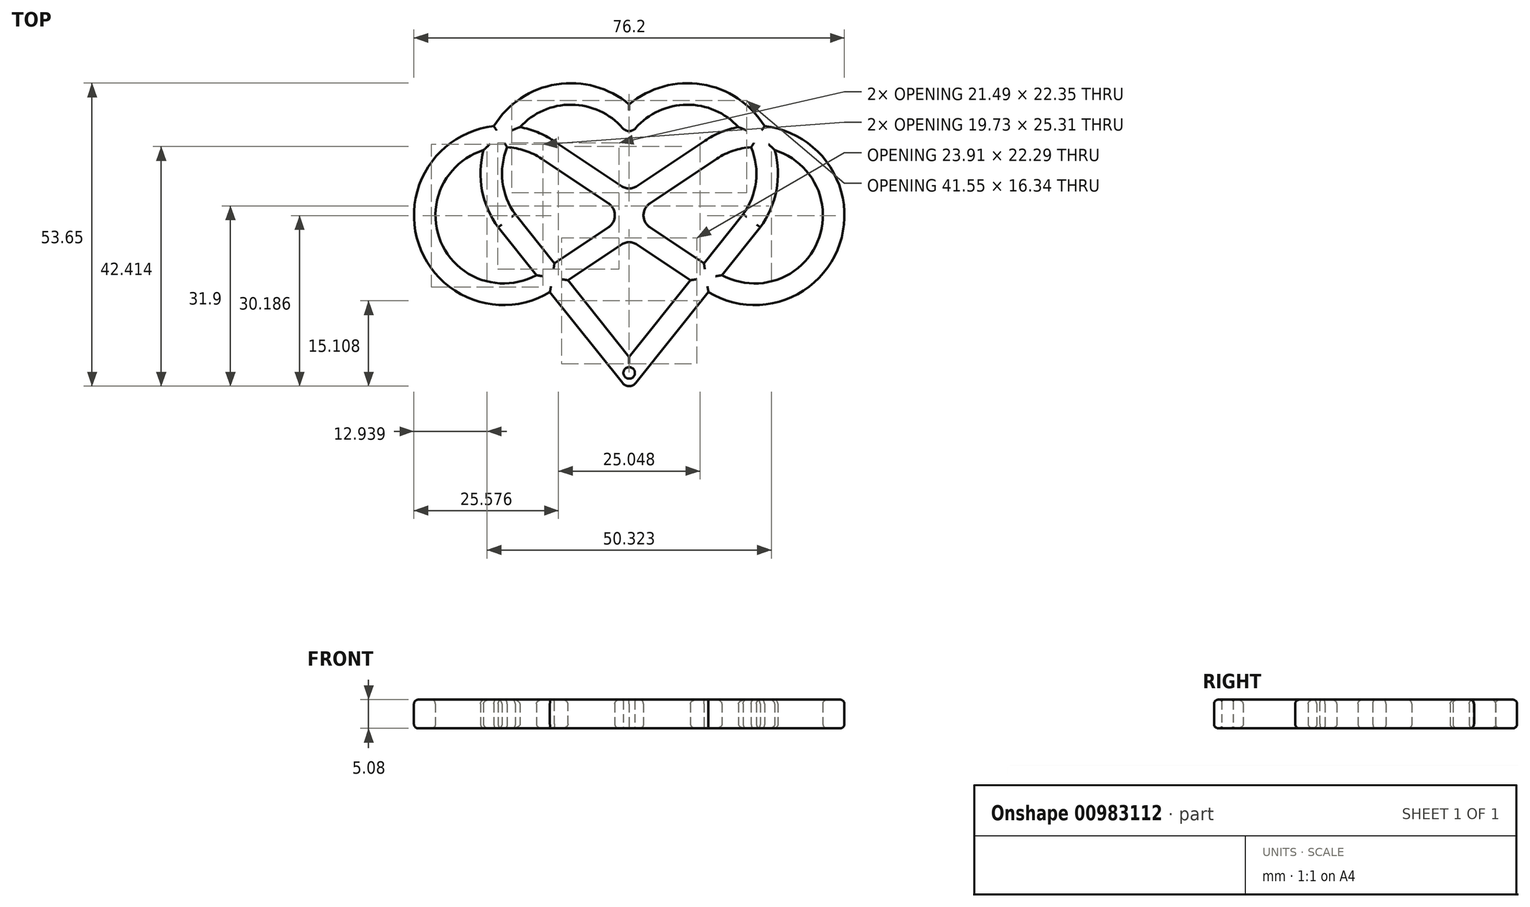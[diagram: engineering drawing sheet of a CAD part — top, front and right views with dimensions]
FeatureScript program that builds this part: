
annotation { "Feature Type Name" : "Feature", "Feature Type Description" : "" }
export const myFeature = defineFeature(function(context is Context, id is Id, definition is map)
    precondition{}
    {
        {
            var Q0;
            Q0=qCreatedBy(makeId("Top.planeOp"),FACE);
            var sketch = newSketch(context, id + "F0", { "sketchPlane" : qUnion([Q0])});
            skLineSegment(sketch, "E0", {"start": v(-12.42, -31.73) * mm, "end": v(-12.42, 29.15) * mm, "construction": true});
            skArc(sketch, "E1.0", {"start": v(-12.42, 24.7) * mm, "mid": v(-33.69, 24.13) * mm, "end": v(-35.61, 2.94) * mm});
            skArc(sketch, "E1.1", {"start": v(-12.42, 24.7) * mm, "mid": v(8.85, 24.13) * mm, "end": v(10.77, 2.94) * mm});
            skLineSegment(sketch, "E1.2", {"start": v(10.77, 2.94) * mm, "end": v(-12.42, -26.1) * mm});
            skLineSegment(sketch, "E1.3", {"start": v(-35.61, 2.94) * mm, "end": v(-12.42, -26.1) * mm});
            skArc(sketch, "E2.0", {"start": v(-12.42, 18.97) * mm, "mid": v(-29.6, 22.55) * mm, "end": v(-32.59, 5.26) * mm});
            skArc(sketch, "E2.1", {"start": v(-12.42, 18.97) * mm, "mid": v(4.75, 22.55) * mm, "end": v(7.75, 5.26) * mm});
            skLineSegment(sketch, "E2.2", {"start": v(7.75, 5.26) * mm, "end": v(-12.42, -20) * mm});
            skLineSegment(sketch, "E2.3", {"start": v(-32.59, 5.26) * mm, "end": v(-12.42, -20) * mm});
            skSolve(sketch);
        }
        {
            var Q0;
            Q0 = qSketchRegion(id + "F0", true);
            extrude(context, id + "F1", {"entities" : qUnion([Q0]), "depth" : 5.08 * mm, "offsetDistance" : 25.4 * mm});
        }
        {
            var Q0;
            Q0=qCreatedBy(makeId("Top.planeOp"),FACE);
            var sketch = newSketch(context, id + "F2", { "sketchPlane" : qUnion([Q0])});
            skArc(sketch, "E3", {"start": v(0.99, -8.13) * mm, "mid": v(25.68, 5.07) * mm, "end": v(0.99, 18.27) * mm});
            skLineSegment(sketch, "E4", {"start": v(-12.42, 45.5) * mm, "end": v(-12.42, -37.96) * mm, "construction": true});
            skArc(sketch, "E5.MirrorC", {"start": v(-25.83, -8.13) * mm, "mid": v(-50.52, 5.07) * mm, "end": v(-25.83, 18.27) * mm});
            skLineSegment(sketch, "E6", {"start": v(-25.83, 18.27) * mm, "end": v(-34.64, 5.07) * mm, "construction": true});
            skLineSegment(sketch, "E7", {"start": v(-34.64, 5.07) * mm, "end": v(9.8, 5.07) * mm, "construction": true});
            skLineSegment(sketch, "E8", {"start": v(-25.83, 18.27) * mm, "end": v(-12.42, 9.31) * mm});
            skLineSegment(sketch, "E9.MirrorCS", {"start": v(-25.83, -8.13) * mm, "end": v(-12.42, 0.82) * mm});
            skLineSegment(sketch, "E10.MirrorCS", {"start": v(0.99, 18.27) * mm, "end": v(-12.42, 9.31) * mm});
            skLineSegment(sketch, "E11.MirrorCS", {"start": v(0.99, -8.13) * mm, "end": v(-12.42, 0.82) * mm});
            skPoint(sketch, "E12.orphan", {"position": v(-18.77, 5.07) * mm});
            skPoint(sketch, "E13.orphan", {"position": v(-6.07, 5.07) * mm});
            skLineSegment(sketch, "E14.0", {"start": v(-27.94, -4.96) * mm, "end": v(-12.93, 5.07) * mm});
            skLineSegment(sketch, "E14.1", {"start": v(-27.94, 15.1) * mm, "end": v(-12.93, 5.07) * mm});
            skLineSegment(sketch, "E14.2", {"start": v(3.1, 15.1) * mm, "end": v(-11.91, 5.07) * mm});
            skArc(sketch, "E14.3", {"start": v(-27.94, -4.96) * mm, "mid": v(-46.7, 5.07) * mm, "end": v(-27.94, 15.1) * mm});
            skArc(sketch, "E14.4", {"start": v(3.1, -4.96) * mm, "mid": v(21.87, 5.07) * mm, "end": v(3.1, 15.1) * mm});
            skLineSegment(sketch, "E14.5", {"start": v(3.1, -4.96) * mm, "end": v(-11.91, 5.07) * mm});
            skSolve(sketch);
        }
        {
            var Q0;
            Q0 = qSketchRegion(id + "F2", true);
            extrude(context, id + "F3", {"entities" : qUnion([Q0]), "operationType" : NewBodyOperationType.ADD, "depth" : 5.08 * mm, "offsetDistance" : 25.4 * mm});
        }
        {
            var Q0;
            Q0=makeQuery(id+"F3.opExtrude","SWEPT_EDGE",EDGE,{"disambiguationData":[OSD([sQuery(id+"F2.wireOp",EDGE,"E14.2"),sQuery(id+"F2.wireOp",EDGE,"E14.5")])]});
            var Q1;
            Q1=makeQuery(id+"F3.opExtrude","SWEPT_EDGE",EDGE,{"disambiguationData":[OSD([sQuery(id+"F2.wireOp",EDGE,"E14.0"),sQuery(id+"F2.wireOp",EDGE,"E14.1")])]});
            var Q2;
            Q2=makeQuery(id+"F3.opExtrude","SWEPT_EDGE",EDGE,{"disambiguationData":[OSD([sQuery(id+"F2.wireOp",EDGE,"E8"),sQuery(id+"F2.wireOp",EDGE,"E10.MirrorCS")])]});
            var Q3;
            Q3=makeQuery(id+"F3.opExtrude","SWEPT_EDGE",EDGE,{"disambiguationData":[OSD([sQuery(id+"F2.wireOp",EDGE,"E9.MirrorCS"),sQuery(id+"F2.wireOp",EDGE,"E11.MirrorCS")])]});
            fillet(context, id + "F4", {"entities" : qUnion([Q0, Q1, Q2, Q3]), "radius" : 2.54 * mm, "tangentPropagation" : true, "allowEdgeOverflow" : false});
        }
        {
            var Q0;
            Q0=makeQuery(id+"F3.boolean.opBoolean","MERGE",FACE,{"derivedFrom":[makeQuery(id+"F1.opExtrude","CAP_FACE",FACE,{"disambiguationData":[OSD([sQuery(id+"F0.wireOp",EDGE,"E1.0"),sQuery(id+"F0.wireOp",EDGE,"E1.1"),sQuery(id+"F0.wireOp",EDGE,"E1.2"),sQuery(id+"F0.wireOp",EDGE,"E1.3"),sQuery(id+"F0.wireOp",EDGE,"E2.0"),sQuery(id+"F0.wireOp",EDGE,"E2.1"),sQuery(id+"F0.wireOp",EDGE,"E2.2"),sQuery(id+"F0.wireOp",EDGE,"E2.3")])],"isStart":false}),makeQuery(id+"F3.opExtrude","CAP_FACE",FACE,{"disambiguationData":[OSD([sQuery(id+"F2.wireOp",EDGE,"E3"),sQuery(id+"F2.wireOp",EDGE,"E5.MirrorC"),sQuery(id+"F2.wireOp",EDGE,"E8"),sQuery(id+"F2.wireOp",EDGE,"E9.MirrorCS"),sQuery(id+"F2.wireOp",EDGE,"E10.MirrorCS"),sQuery(id+"F2.wireOp",EDGE,"E11.MirrorCS"),sQuery(id+"F2.wireOp",EDGE,"E14.0"),sQuery(id+"F2.wireOp",EDGE,"E14.1"),sQuery(id+"F2.wireOp",EDGE,"E14.2"),sQuery(id+"F2.wireOp",EDGE,"E14.3"),sQuery(id+"F2.wireOp",EDGE,"E14.4"),sQuery(id+"F2.wireOp",EDGE,"E14.5")])],"isStart":false})]});
            var Q1;
            Q1=makeQuery(id+"F3.boolean.opBoolean","MERGE",FACE,{"derivedFrom":[makeQuery(id+"F1.opExtrude","CAP_FACE",FACE,{"disambiguationData":[OSD([sQuery(id+"F0.wireOp",EDGE,"E1.0"),sQuery(id+"F0.wireOp",EDGE,"E1.1"),sQuery(id+"F0.wireOp",EDGE,"E1.2"),sQuery(id+"F0.wireOp",EDGE,"E1.3"),sQuery(id+"F0.wireOp",EDGE,"E2.0"),sQuery(id+"F0.wireOp",EDGE,"E2.1"),sQuery(id+"F0.wireOp",EDGE,"E2.2"),sQuery(id+"F0.wireOp",EDGE,"E2.3")])],"isStart":true}),makeQuery(id+"F3.opExtrude","CAP_FACE",FACE,{"disambiguationData":[OSD([sQuery(id+"F2.wireOp",EDGE,"E3"),sQuery(id+"F2.wireOp",EDGE,"E5.MirrorC"),sQuery(id+"F2.wireOp",EDGE,"E8"),sQuery(id+"F2.wireOp",EDGE,"E9.MirrorCS"),sQuery(id+"F2.wireOp",EDGE,"E10.MirrorCS"),sQuery(id+"F2.wireOp",EDGE,"E11.MirrorCS"),sQuery(id+"F2.wireOp",EDGE,"E14.0"),sQuery(id+"F2.wireOp",EDGE,"E14.1"),sQuery(id+"F2.wireOp",EDGE,"E14.2"),sQuery(id+"F2.wireOp",EDGE,"E14.3"),sQuery(id+"F2.wireOp",EDGE,"E14.4"),sQuery(id+"F2.wireOp",EDGE,"E14.5")])],"isStart":true})]});
            fillet(context, id + "F5", {"entities" : qUnion([Q0, Q1]), "radius" : 0.76 * mm, "tangentPropagation" : true, "allowEdgeOverflow" : false});
        }
        {
            var Q0;
            Q0=qCreatedBy(makeId("Top.planeOp"),FACE);
            var sketch = newSketch(context, id + "F6", { "sketchPlane" : qUnion([Q0])});
            skCircle(sketch, "E15", {"center": v(-12.42, -22.83) * mm, "radius": 1.02 * mm});
            skSolve(sketch);
        }
        {
            var Q0;
            Q0 = qSketchRegion(id + "F6", true);
            extrude(context, id + "F7", {"entities" : qUnion([Q0]), "operationType" : NewBodyOperationType.REMOVE, "endBound" : BoundingType.THROUGH_ALL, "depth" : 25.4 * mm, "offsetDistance" : 25.4 * mm});
        }
        {
            var Q0;
            Q0=makeQuery(id+"F7.boolean.opBoolean","COPY",FACE,{"derivedFrom":makeQuery(id+"F7.opExtrude","SWEPT_FACE",FACE,{"disambiguationData":[OSD([sQuery(id+"F6.wireOp",EDGE,"E15")])]})});
            fillet(context, id + "F8", {"entities" : qUnion([Q0]), "radius" : 0.25 * mm, "tangentPropagation" : true, "allowEdgeOverflow" : false});
        }
        {
            var Q0;
            Q0=makeQuery(id+"F1.opExtrude","SWEPT_EDGE",EDGE,{"disambiguationData":[OSD([sQuery(id+"F0.wireOp",EDGE,"E2.0"),sQuery(id+"F0.wireOp",EDGE,"E2.1")])]});
            var Q1;
            Q1=makeQuery(id+"F1.opExtrude","SWEPT_EDGE",EDGE,{"disambiguationData":[OSD([sQuery(id+"F0.wireOp",EDGE,"E1.2"),sQuery(id+"F0.wireOp",EDGE,"E1.3")])]});
            fillet(context, id + "F9", {"entities" : qUnion([Q0, Q1]), "radius" : 1.52 * mm, "tangentPropagation" : true, "allowEdgeOverflow" : false});
        }
    });
